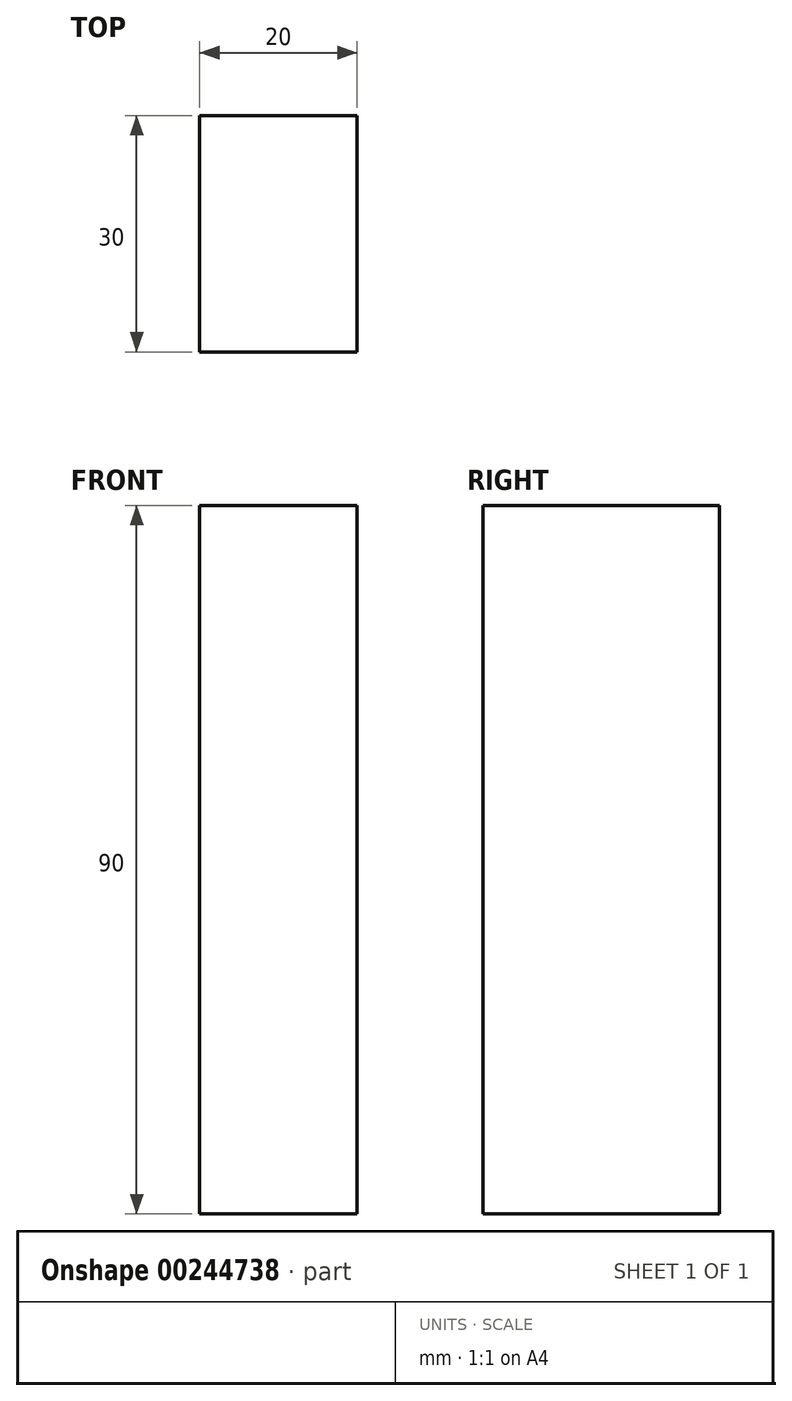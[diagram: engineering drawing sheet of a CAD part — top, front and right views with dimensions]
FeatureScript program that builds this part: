
annotation { "Feature Type Name" : "Feature", "Feature Type Description" : "" }
export const myFeature = defineFeature(function(context is Context, id is Id, definition is map)
    precondition{}
    {
        {
            var Q0;
            Q0=qCreatedBy(makeId("Top.planeOp"),FACE);
            var sketch = newSketch(context, id + "F0", { "sketchPlane" : qUnion([Q0])});
            skLineSegment(sketch, "E0.bottom", {"start": v(0, 0) * mm, "end": v(20, 0) * mm});
            skLineSegment(sketch, "E0.top", {"start": v(0, 30) * mm, "end": v(20, 30) * mm});
            skLineSegment(sketch, "E0.left", {"start": v(0, 0) * mm, "end": v(0, 30) * mm});
            skLineSegment(sketch, "E0.right", {"start": v(20, 0) * mm, "end": v(20, 30) * mm});
            skSolve(sketch);
        }
        {
            var Q0;
            Q0 = qSketchRegion(id + "F0", true);
            extrude(context, id + "F1", {"entities" : qUnion([Q0]), "depth" : 90 * mm});
        }
    });
